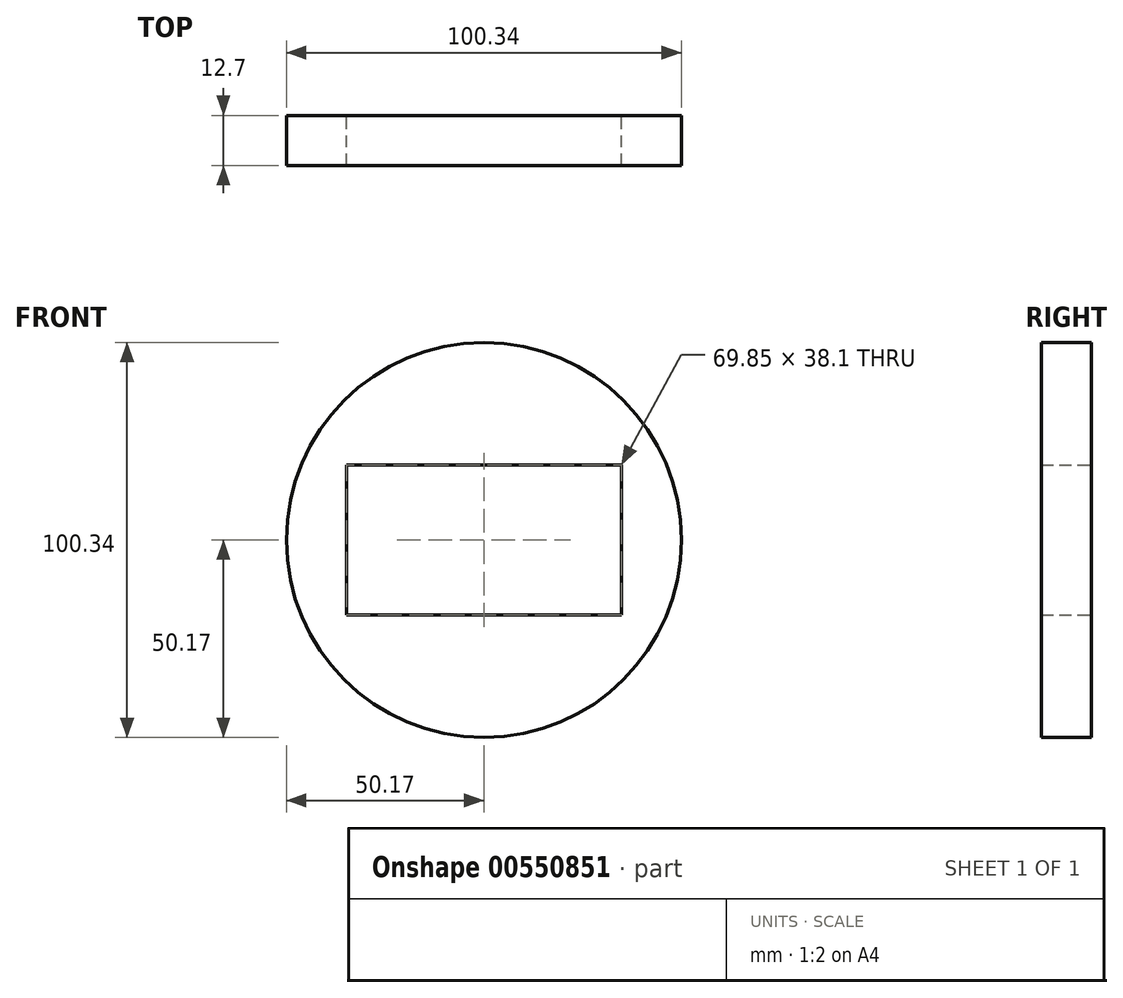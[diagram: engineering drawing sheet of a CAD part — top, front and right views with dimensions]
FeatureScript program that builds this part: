
annotation { "Feature Type Name" : "Feature", "Feature Type Description" : "" }
export const myFeature = defineFeature(function(context is Context, id is Id, definition is map)
    precondition{}
    {
        {
            var Q0;
            Q0=qCreatedBy(makeId("Front.planeOp"),FACE);
            var sketch = newSketch(context, id + "F0", { "sketchPlane" : qUnion([Q0])});
            skCircle(sketch, "E0", {"center": v(0, 0) * mm, "radius": 50.17 * mm});
            skLineSegment(sketch, "E1.bottom", {"start": v(34.92, 19.05) * mm, "end": v(-34.93, 19.05) * mm});
            skLineSegment(sketch, "E1.top", {"start": v(34.93, -19.05) * mm, "end": v(-34.93, -19.05) * mm});
            skLineSegment(sketch, "E1.left", {"start": v(34.92, 19.05) * mm, "end": v(34.93, -19.05) * mm});
            skLineSegment(sketch, "E1.right", {"start": v(-34.93, 19.05) * mm, "end": v(-34.93, -19.05) * mm});
            skSolve(sketch);
        }
        {
            var Q0;
            Q0=makeQuery(id+"F0.imprint","IMPRINT",FACE,{"disambiguationData":[TD([[makeQuery(id+"F0.imprint","IMPRINT",EDGE,{"derivedFrom":sQuery(id+"F0.wireOp",EDGE,"E0")}),1.0]])]});
            extrude(context, id + "F1", {"entities" : qUnion([Q0]), "depth" : 12.7 * mm, "offsetDistance" : 25.4 * mm});
        }
    });
